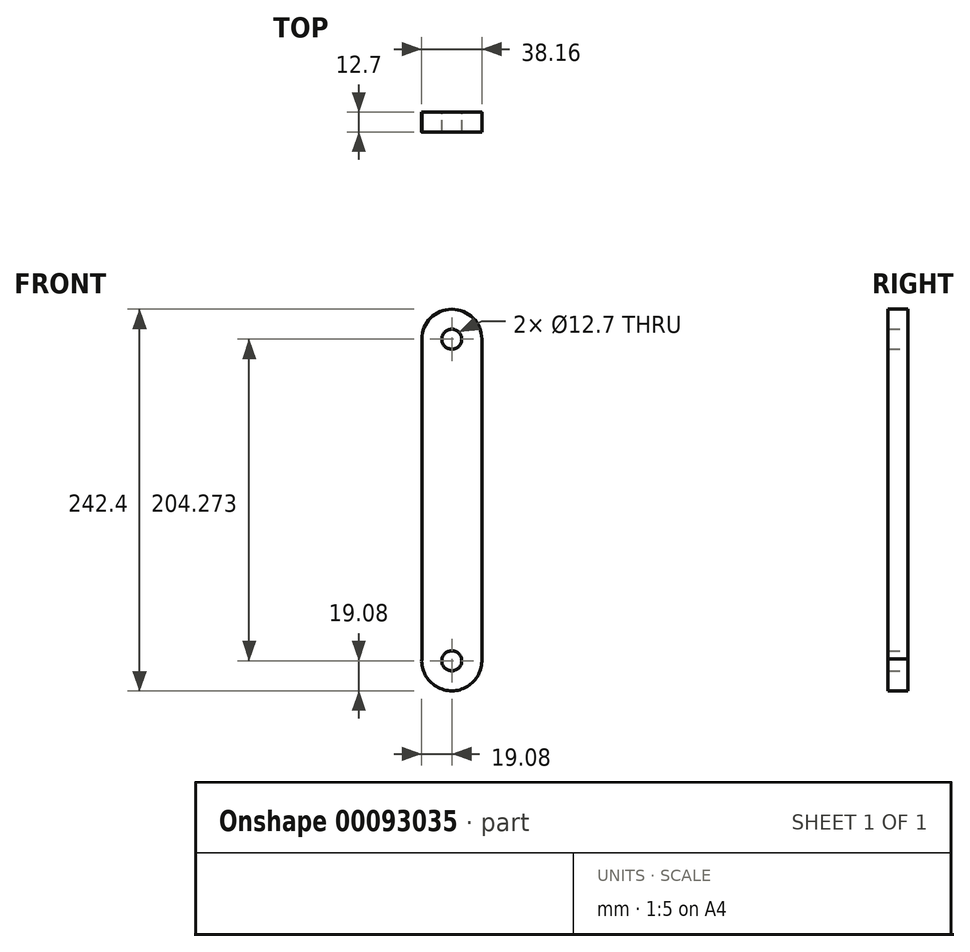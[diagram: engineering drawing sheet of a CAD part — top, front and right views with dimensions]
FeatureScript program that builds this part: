
annotation { "Feature Type Name" : "Feature", "Feature Type Description" : "" }
export const myFeature = defineFeature(function(context is Context, id is Id, definition is map)
    precondition{}
    {
        {
            var Q0;
            Q0=qCreatedBy(makeId("Front.planeOp"),FACE);
            var sketch = newSketch(context, id + "F0", { "sketchPlane" : qUnion([Q0])});
            skArc(sketch, "E0", {"start": v(-33.72, 156.56) * mm, "mid": v(-52.77, 175.61) * mm, "end": v(-71.82, 156.56) * mm});
            skLineSegment(sketch, "E1", {"start": v(-71.82, 156.56) * mm, "end": v(-71.82, -46.64) * mm});
            skLineSegment(sketch, "E2", {"start": v(-33.72, 156.56) * mm, "end": v(-33.72, -46.64) * mm});
            skLineSegment(sketch, "E3", {"start": v(-52.77, 156.56) * mm, "end": v(-33.72, 156.56) * mm});
            skPoint(sketch, "E4.MirrorCS.end.orphan", {"position": v(-71.82, 156.56) * mm});
            skPoint(sketch, "E4.MirrorCS.start.orphan", {"position": v(-33.72, 156.56) * mm});
            skArc(sketch, "E5", {"start": v(-71.82, -46.64) * mm, "mid": v(-52.77, -66.8) * mm, "end": v(-33.72, -46.64) * mm});
            skPoint(sketch, "E5.third.point", {"position": v(-62.98, -31.6) * mm});
            skCircle(sketch, "E6", {"center": v(-52.77, 156.56) * mm, "radius": 6.35 * mm});
            skCircle(sketch, "E7", {"center": v(-52.77, -47.71) * mm, "radius": 6.35 * mm});
            skSolve(sketch);
        }
        {
            var Q0;
            Q0=makeQuery(id+"F0.imprint","IMPRINT",FACE,{"disambiguationData":[TD([[makeQuery(id+"F0.imprint","IMPRINT",EDGE,{"derivedFrom":sQuery(id+"F0.wireOp",EDGE,"E0")}),1.0]])]});
            extrude(context, id + "F1", {"entities" : qUnion([Q0]), "depth" : 12.7 * mm});
        }
    });
